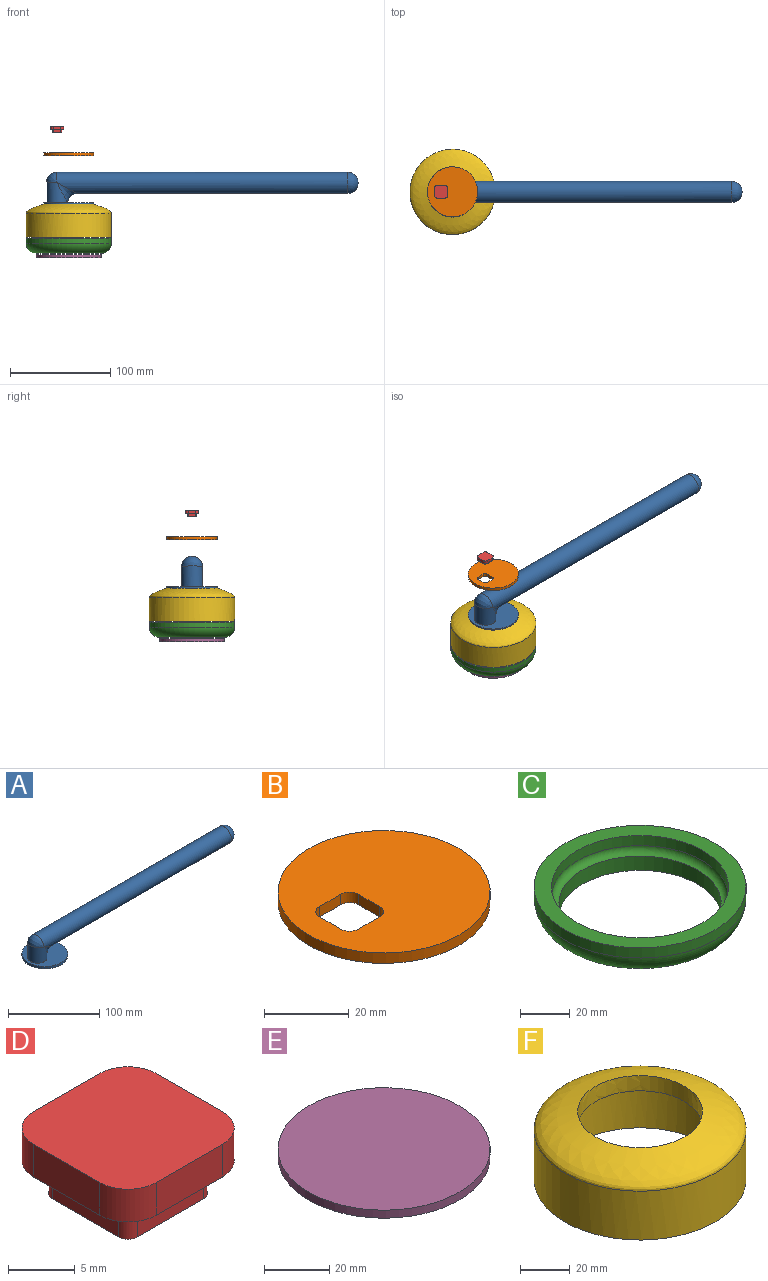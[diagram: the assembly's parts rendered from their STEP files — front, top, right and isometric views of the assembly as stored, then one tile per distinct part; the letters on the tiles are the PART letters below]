
ASSEMBLY  parts=6 mates=6
PART A: 9 faces, bbox 313.5x50x33.5 mm
  f0: cylinder r=25mm len=50mm, axis (0,0,-1), area 471.2mm2, adj f1,f2
  f1: plane 50x50mm, normal (0,0,1), area 1617.1mm2, adj f0,f5
  f2: plane 50x50mm, normal (0,0,-1), area 1963.5mm2, adj f0
  f3: plane 1x1mm, normal (1,0,0), area 0.8mm2, adj f8
  f4: cylinder r=10.5mm len=291mm, axis (1,0,0), area 18733.3mm2, adj f6,f7,f8
  f5: cylinder r=10.5mm len=21mm, axis (0,0,1), area 920.5mm2, adj f1,f6,f7
  f6: bspline ~21x20mm, area 373.7mm2, adj f4,f5
  f7: bspline ~21x10.5mm, area 316.4mm2, adj f4,f5
  f8: torus R=0.5mm, axis (1,0,0), area 677.7mm2, adj f3,f4
PART B: 11 faces, bbox 50x50x3 mm
  f0: plane 50x50mm, normal (0,0,1), area 1802.2mm2, adj f2,f3,f4,f5,f6,f7,f8,f9
  f1: plane 50x50mm, normal (0,0,-1), area 1802.2mm2, adj f2,f3,f4,f5,f6,f7,f8,f9
  f2: cylinder r=25mm len=50mm, axis (0,0,-1), area 471.2mm2, adj f0,f1
  f3: plane 7x3mm, normal (0,-1,0), area 21mm2, adj f0,f1,f4,f10
  f4: cylinder r=3mm len=3mm, axis (0,0,1), area 14.1mm2, adj f0,f1,f3,f5
  f5: plane 7x3mm, normal (1,0,0), area 21mm2, adj f0,f1,f4,f6
  f6: cylinder r=3mm len=3mm, axis (0,0,1), area 14.1mm2, adj f0,f1,f5,f7
  f7: plane 7x3mm, normal (0,1,0), area 21mm2, adj f0,f1,f6,f8
  f8: cylinder r=3mm len=3mm, axis (0,0,1), area 14.1mm2, adj f0,f1,f7,f9
  f9: plane 7x3mm, normal (-1,0,0), area 21mm2, adj f0,f1,f8,f10
  f10: cylinder r=3mm len=3mm, axis (0,0,1), area 14.1mm2, adj f0,f1,f3,f9
PART C: 6 faces, bbox 92x92x17.1 mm
  f0: cylinder r=42.5mm len=85mm, axis (0,0,1), area 1335.2mm2, adj f1,f2
  f1: plane 85x85mm, normal (0,0,1), area 1715.3mm2, adj f0,f3
  f2: torus R=32.5mm, axis (0,0,1), area 3835.9mm2, adj f0,f5
  f3: cylinder r=35.5mm len=71mm, axis (0,0,1), area 1115.3mm2, adj f1,f4
  f4: torus R=32.5mm, axis (0,0,1), area 1018.8mm2, adj f3,f5
  f5: cylinder r=32.5mm len=65mm, axis (0,0,1), area 1429.4mm2, adj f2,f4
PART D: 19 faces, bbox 13x13x6 mm
  f0: plane 7x3mm, normal (-1,0,0), area 21mm2, adj f1,f7,f8,f9
  f1: cylinder r=3mm len=3mm, axis (0,0,-1), area 14.1mm2, adj f0,f2,f8,f9
  f2: plane 7x3mm, normal (0,-1,0), area 21mm2, adj f1,f3,f8,f9
  f3: cylinder r=3mm len=3mm, axis (0,0,-1), area 14.1mm2, adj f2,f4,f8,f9
  f4: plane 7x3mm, normal (1,0,0), area 21mm2, adj f3,f5,f8,f9
  f5: cylinder r=3mm len=3mm, axis (0,0,-1), area 14.1mm2, adj f4,f6,f8,f9
  f6: plane 7x3mm, normal (0,1,0), area 21mm2, adj f5,f7,f8,f9
  f7: cylinder r=3mm len=3mm, axis (0,0,-1), area 14.1mm2, adj f0,f6,f8,f9
  f8: plane 13x13mm, normal (0,0,1), area 161.3mm2, adj f0,f1,f2,f3,f4,f5,f6,f7
  f9: plane 13x13mm, normal (0,0,-1), area 81.1mm2, adj f0,f1,f2,f3,f4,f5,f6,f7
  f10: plane 7x3mm, normal (1,0,0), area 21mm2, adj f9,f11,f17,f18
  f11: cylinder r=1mm len=3mm, axis (0,0,1), area 4.7mm2, adj f9,f10,f12,f18
  f12: plane 7x3mm, normal (0,-1,0), area 21mm2, adj f9,f11,f13,f18
  f13: cylinder r=1mm len=3mm, axis (0,0,1), area 4.7mm2, adj f9,f12,f14,f18
  f14: plane 7x3mm, normal (-1,0,0), area 21mm2, adj f9,f13,f15,f18
  f15: cylinder r=1mm len=3mm, axis (0,0,1), area 4.7mm2, adj f9,f14,f16,f18
  f16: plane 7x3mm, normal (0,1,0), area 21mm2, adj f9,f15,f17,f18
  f17: cylinder r=1mm len=3mm, axis (0,0,1), area 4.7mm2, adj f9,f10,f16,f18
  f18: plane 9x9mm, normal (0,0,-1), area 80.1mm2, adj f10,f11,f12,f13,f14,f15,f16,f17
PART E: 3 faces, bbox 65x65x3 mm
  f0: cylinder r=32.5mm len=65mm, axis (0,0,-1), area 612.6mm2, adj f1,f2
  f1: plane 65x65mm, normal (0,0,1), area 3318.3mm2, adj f0
  f2: plane 65x65mm, normal (0,0,-1), area 3318.3mm2, adj f0
PART F: 6 faces, bbox 99.2x99.2x47.2 mm
  f0: cylinder r=42.5mm len=85mm, axis (0,0,-1), area 6408.8mm2, adj f1,f2
  f1: plane 85x85mm, normal (0,0,-1), area 1737.6mm2, adj f0,f4
  f2: bspline ~85x85mm, area 4395.7mm2, adj f0,f5
  f3: offset ~96.54x96.54mm, area 2115.4mm2, adj f4,f5
  f4: cylinder r=35.4mm len=70.8mm, axis (0,0,-1), area 4805.2mm2, adj f1,f3
  f5: extruded ~50x50mm, area 1172.1mm2, adj f2,f3
PLACE A t=(23.96,-10.46,98.29)mm
PLACE B t=(23.96,-10.46,148.3)mm
PLACE C t=(23.96,-10.46,51.12)mm
PLACE D t=(5.96,-3.96,174.97)mm
PLACE E t=(23.96,-10.46,46.43)mm
PLACE F t=(23.96,-10.46,67.01)mm
MATE slider E.f0 <-> C.f0  axis (0,0,1) through (23.96,-10.46,49.43)mm
MATE slider A.f0 <-> F.f0  axis (0,0,1) through (23.96,-10.46,101.29)mm
MATE planar D.f0 <-> B.f5  axis (-1,0,0) through (5.96,-10.46,176.47)mm
MATE slider C.f0 <-> B.f2  axis (0,0,1) through (23.96,-10.46,51.12)mm
MATE planar B.f3 <-> D.f6  axis (0,-1,0) through (12.46,-3.96,149.8)mm
MATE slider F.f0 <-> C.f0  axis (0,0,-1) through (23.96,-10.46,67.01)mm
